# Revit family: Doors_Sliding-Doors_US-Bullet-Proofing_USAD1000-Single-1
name_source: partatom
category: Doors
units: mm (PartAtom-declared; Revit-internal decimal feet)

## family parameters
Always vertical = Yes
Cut with Voids When Loaded = Yes
Host = Wall
OmniClass Number = 23.30.10.00
OmniClass Title = Doors
Room Calculation Point = No
Shared = No

## types (1)
- 6' 4" x 7'
    Assembly Code = B2030
    Description = USAD 1000 – Forced Entry/Bullet/Blast Resistant Aluminum Door
    Function = Interior
    Gap = 0' - 0 3/8"
    Glass Thickness = 0' - 1 7/32"
    Glass Thickness Note = The glazing system can be capable of accepting various thickness, ranging from 1.3125 inch to 2.125 inch
    Hardware Note = Standard door hardware: Heavy-duty continuous hinge, deadbolt lockset with high security cylinder, LCN closer, threshold and push/pull handles. Numerous hardware options are available to meet access and security needs; please consult factory for further information.
    Height = 7' - 0"
    Manufacturer = US Bullet Proofing
    Model = USAD 1000 - Single - Slide
    Product Guid = f74ac6bd-064f-438b-91a9-6330e71e0abc
    Product data url = https://www.bimobject.com
    Product url = https://www.usbulletproofing.com
    Rough Height = 7' - 0 3/8"
    Rough Width = 6' - 4 3/4"
    Thickness = 0' - 2 3/4"
    URL = https://www.usbulletproofing.com
    Wall Closure = By host
    Width = 6' - 4"
    z_Glass Thickness Control = 0' - 1 7/32"

## geometry (parser evidence)
native form markers: Sweep x2
no freeform markers — native parametric forms only
